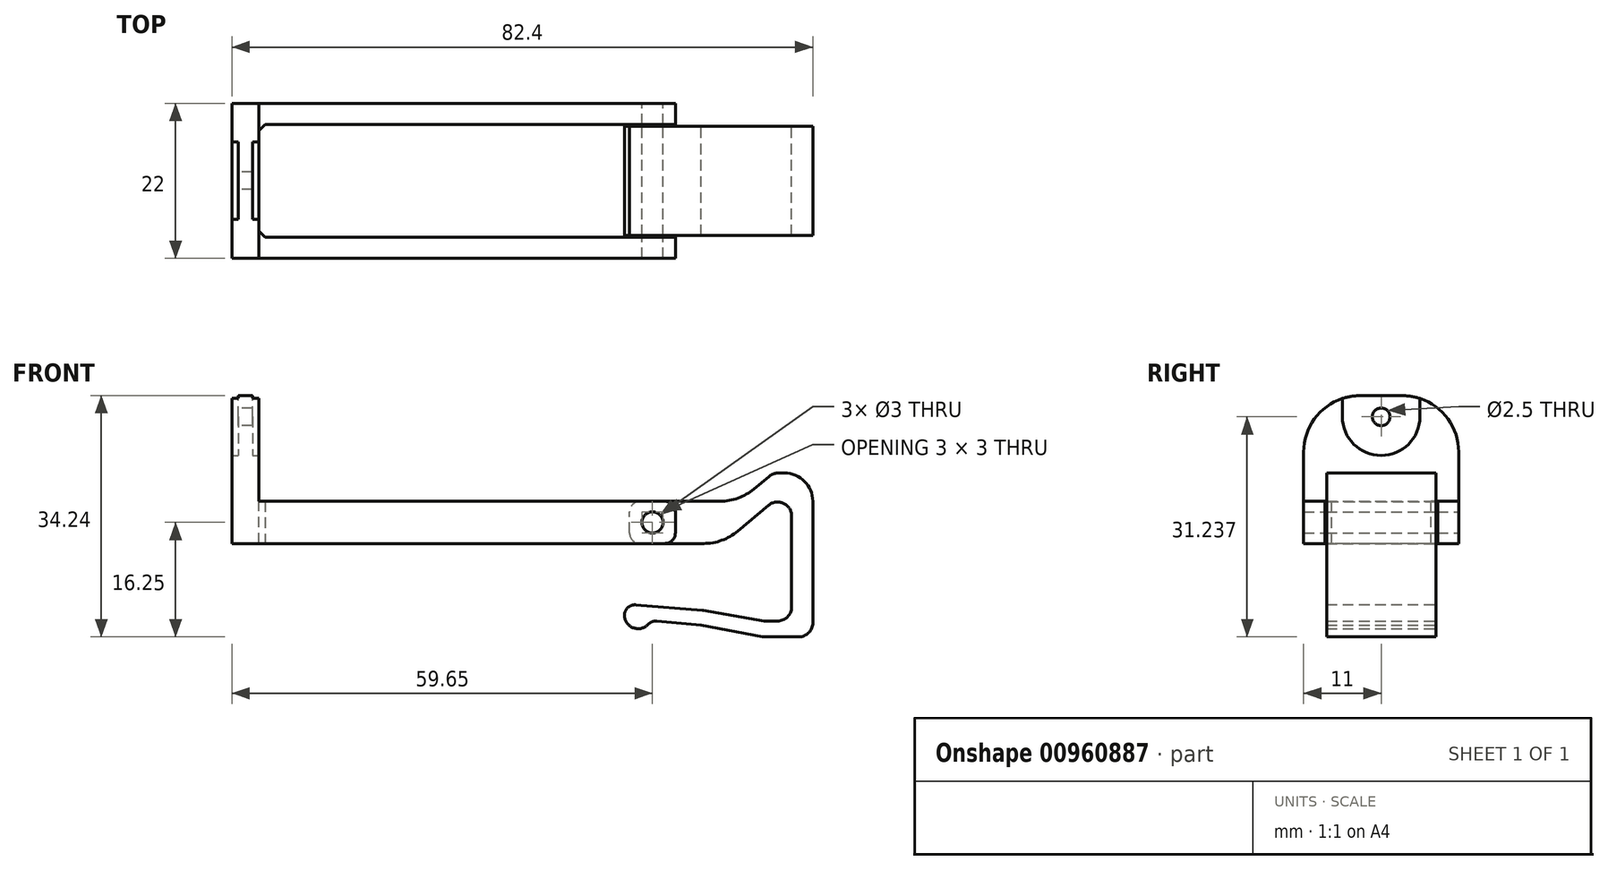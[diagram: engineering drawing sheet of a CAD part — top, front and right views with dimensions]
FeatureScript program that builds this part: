
annotation { "Feature Type Name" : "Feature", "Feature Type Description" : "" }
export const myFeature = defineFeature(function(context is Context, id is Id, definition is map)
    precondition{}
    {
        {
            var Q0;
            Q0=qCreatedBy(makeId("Right.planeOp"),FACE);
            var sketch = newSketch(context, id + "F0", { "sketchPlane" : qUnion([Q0])});
            skCircle(sketch, "E0", {"center": v(0, 17.99) * mm, "radius": 1.25 * mm});
            skLineSegment(sketch, "E1.bottom", {"start": v(-12.5, -0.01) * mm, "end": v(12.5, -0.01) * mm});
            skLineSegment(sketch, "E1.left", {"start": v(-11, -0.01) * mm, "end": v(-11, 12.99) * mm});
            skLineSegment(sketch, "E1.right", {"start": v(11, -0.01) * mm, "end": v(11, 12.99) * mm});
            skPoint(sketch, "E1.middle", {"position": v(0, 13) * mm});
            skLineSegment(sketch, "E2", {"start": v(12.5, 12.99) * mm, "end": v(-12.5, 12.99) * mm, "construction": true});
            skLineSegment(sketch, "E3", {"start": v(0, 4.99) * mm, "end": v(0, 20.99) * mm, "construction": true});
            skLineSegment(sketch, "E4.0", {"start": v(4.5, 4.99) * mm, "end": v(4.5, 20.99) * mm, "construction": true});
            skLineSegment(sketch, "E5.MirrorCS", {"start": v(-4.5, 4.99) * mm, "end": v(-4.5, 20.99) * mm, "construction": true});
            skLineSegment(sketch, "E6", {"start": v(5.5, 17.99) * mm, "end": v(-5.5, 17.99) * mm, "construction": true});
            skLineSegment(sketch, "E7", {"start": v(-5.5, 17.99) * mm, "end": v(-5.5, 20.92) * mm});
            skLineSegment(sketch, "E8.MirrorCS", {"start": v(5.5, 17.99) * mm, "end": v(5.5, 20.92) * mm});
            skArc(sketch, "E9", {"start": v(5.5, 17.99) * mm, "mid": v(0, 12.49) * mm, "end": v(-5.5, 17.99) * mm});
            skLineSegment(sketch, "E10", {"start": v(4.5, 20.99) * mm, "end": v(-4.5, 20.99) * mm});
            skPoint(sketch, "E11.middle", {"position": v(0, -0.01) * mm});
            skLineSegment(sketch, "E12.bottom", {"start": v(-20, 27.99) * mm, "end": v(20, 27.99) * mm});
            skLineSegment(sketch, "E12.top", {"start": v(-20, -7.01) * mm, "end": v(20, -7.01) * mm});
            skLineSegment(sketch, "E12.left", {"start": v(-20, 27.99) * mm, "end": v(-20, -7.01) * mm});
            skLineSegment(sketch, "E12.right", {"start": v(20, 27.99) * mm, "end": v(20, -7.01) * mm});
            skCircle(sketch, "E13", {"center": v(0, 0) * mm, "radius": 2.5 * mm, "construction": true});
            skArc(sketch, "E14", {"start": v(-11, 12.99) * mm, "mid": v(-9.17, 18.14) * mm, "end": v(-4.5, 20.99) * mm});
            skArc(sketch, "E15", {"start": v(11, 12.99) * mm, "mid": v(9.17, 18.14) * mm, "end": v(4.5, 20.99) * mm});
            skSolve(sketch);
        }
        {
            var Q0;
            Q0=qCreatedBy(makeId("Front.planeOp"),FACE);
            var sketch = newSketch(context, id + "F1", { "sketchPlane" : qUnion([Q0])});
            skPoint(sketch, "E16.middle", {"position": v(0, 8) * mm});
            skCircle(sketch, "E17", {"center": v(57.75, 3) * mm, "radius": 1.5 * mm});
            skArc(sketch, "E18", {"start": v(59.5, 0) * mm, "mid": v(60.56, 0.44) * mm, "end": v(61, 1.5) * mm});
            skArc(sketch, "E19.MirrorCS", {"start": v(59.5, 6) * mm, "mid": v(60.56, 5.56) * mm, "end": v(61, 4.5) * mm});
            skLineSegment(sketch, "E20", {"start": v(2, 6) * mm, "end": v(2, 21) * mm});
            skLineSegment(sketch, "E21", {"start": v(2, 21) * mm, "end": v(-2, 21) * mm});
            skLineSegment(sketch, "E22", {"start": v(-2, 21) * mm, "end": v(-2, 6) * mm});
            skLineSegment(sketch, "E23", {"start": v(-6.5, 0) * mm, "end": v(59.5, 0) * mm});
            skLineSegment(sketch, "E24", {"start": v(61, 4.5) * mm, "end": v(61, 1.5) * mm});
            skCircle(sketch, "E25", {"center": v(-4.75, 3) * mm, "radius": 1.5 * mm});
            skArc(sketch, "E26", {"start": v(-6.5, 6) * mm, "mid": v(-7.56, 5.56) * mm, "end": v(-8, 4.5) * mm});
            skArc(sketch, "E27.MirrorCS", {"start": v(-6.5, 0) * mm, "mid": v(-7.56, 0.44) * mm, "end": v(-8, 1.5) * mm});
            skLineSegment(sketch, "E28", {"start": v(-8, 1.5) * mm, "end": v(-8, 4.5) * mm});
            skLineSegment(sketch, "E29", {"start": v(59.5, 6) * mm, "end": v(2, 6) * mm});
            skLineSegment(sketch, "E30", {"start": v(-2, 6) * mm, "end": v(-6.5, 6) * mm});
            skSolve(sketch);
        }
        {
            var Q0;
            Q0=qCreatedBy(makeId("Top.planeOp"),FACE);
            var sketch = newSketch(context, id + "F2", { "sketchPlane" : qUnion([Q0])});
            skLineSegment(sketch, "E31.left", {"start": v(-2, 12.5) * mm, "end": v(-2, -12.5) * mm});
            skPoint(sketch, "E31.middle", {"position": v(56.25, 0) * mm});
            skLineSegment(sketch, "E32.0", {"start": v(2, 12.5) * mm, "end": v(2, -12.5) * mm});
            skLineSegment(sketch, "E33", {"start": v(-2, 0) * mm, "end": v(18.5, 0) * mm, "construction": true});
            skLineSegment(sketch, "E34.0", {"start": v(61, 11) * mm, "end": v(61, 8) * mm});
            skLineSegment(sketch, "E35.trimOffspring", {"start": v(61, -8) * mm, "end": v(61, -11) * mm});
            skLineSegment(sketch, "E36.bottom", {"start": v(69, 17.5) * mm, "end": v(-13, 17.5) * mm});
            skLineSegment(sketch, "E36.top", {"start": v(69, -17.5) * mm, "end": v(-13, -17.5) * mm});
            skLineSegment(sketch, "E36.left", {"start": v(69, 17.5) * mm, "end": v(69, -17.5) * mm});
            skLineSegment(sketch, "E36.right", {"start": v(-13, 17.5) * mm, "end": v(-13, -17.5) * mm});
            skPoint(sketch, "E36.middle", {"position": v(23, 0) * mm});
            skCircle(sketch, "E37", {"center": v(0, 0) * mm, "radius": 2.5 * mm, "construction": true});
            skLineSegment(sketch, "E38.0", {"start": v(61, -11) * mm, "end": v(-7.9, -11) * mm});
            skLineSegment(sketch, "E38.1", {"start": v(61, 11) * mm, "end": v(-7.9, 11) * mm});
            skLineSegment(sketch, "E38.2", {"start": v(-7.9, 8) * mm, "end": v(-2, 8) * mm});
            skLineSegment(sketch, "E38.3", {"start": v(-7.9, -8) * mm, "end": v(-2, -8) * mm});
            skCircle(sketch, "E38.4", {"center": v(23, 0) * mm, "radius": 2.5 * mm, "construction": true});
            skLineSegment(sketch, "E39", {"start": v(-7.9, 11) * mm, "end": v(-7.9, 8) * mm});
            skLineSegment(sketch, "E40", {"start": v(-7.9, -8) * mm, "end": v(-7.9, -11) * mm});
            skLineSegment(sketch, "E41", {"start": v(2, 8) * mm, "end": v(61, 8) * mm});
            skLineSegment(sketch, "E42", {"start": v(2, -8) * mm, "end": v(61, -8) * mm});
            skSolve(sketch);
        }
        {
            var Q0;
            Q0=qCreatedBy(makeId("Front.planeOp"),FACE);
            var sketch = newSketch(context, id + "F3", { "sketchPlane" : qUnion([Q0])});
            skCircle(sketch, "E43.0", {"center": v(57.75, 3) * mm, "radius": 1.5 * mm});
            skLineSegment(sketch, "E44.0", {"start": v(56, 0) * mm, "end": v(67.75, 0) * mm});
            skArc(sketch, "E44.1", {"start": v(56, 0) * mm, "mid": v(54.94, 0.44) * mm, "end": v(54.5, 1.5) * mm});
            skLineSegment(sketch, "E44.2", {"start": v(54.5, 1.5) * mm, "end": v(54.5, 4.5) * mm});
            skArc(sketch, "E44.3", {"start": v(56, 6) * mm, "mid": v(54.94, 5.56) * mm, "end": v(54.5, 4.5) * mm});
            skLineSegment(sketch, "E44.4", {"start": v(80.5, -13.25) * mm, "end": v(80.5, 10) * mm});
            skLineSegment(sketch, "E45", {"start": v(77.5, 8.18) * mm, "end": v(77.5, -11) * mm});
            skLineSegment(sketch, "E46", {"start": v(74.83, 10) * mm, "end": v(80.5, 10) * mm});
            skLineSegment(sketch, "E47", {"start": v(67.75, 0) * mm, "end": v(77.5, 8.18) * mm});
            skLineSegment(sketch, "E48", {"start": v(70.07, 6) * mm, "end": v(56, 6) * mm});
            skLineSegment(sketch, "E49", {"start": v(74.83, 10) * mm, "end": v(70.07, 6) * mm});
            skLineSegment(sketch, "E50", {"start": v(73.75, -11) * mm, "end": v(77.5, -11) * mm});
            skLineSegment(sketch, "E51", {"start": v(73.5, -13.25) * mm, "end": v(80.5, -13.25) * mm});
            skLineSegment(sketch, "E52", {"start": v(73.75, -11) * mm, "end": v(64.88, -9.48) * mm});
            skLineSegment(sketch, "E53", {"start": v(73.5, -13.25) * mm, "end": v(64.61, -11.61) * mm});
            skArc(sketch, "E54", {"start": v(54.5, -8.62) * mm, "mid": v(54.52, -11.68) * mm, "end": v(57.49, -10.93) * mm});
            skLineSegment(sketch, "E55", {"start": v(64.88, -9.48) * mm, "end": v(54.5, -8.62) * mm});
            skLineSegment(sketch, "E56", {"start": v(64.61, -11.61) * mm, "end": v(57.49, -10.93) * mm});
            skSolve(sketch);
        }
        {
            var Q0;
            Q0=makeQuery(id+"F1.imprint","IMPRINT",FACE,{"disambiguationData":[TD([[makeQuery(id+"F1.imprint","IMPRINT",EDGE,{"derivedFrom":sQuery(id+"F1.wireOp",EDGE,"E17")}),-1.0]])]});
            extrude(context, id + "F4", {"entities" : qUnion([Q0]), "endBound" : BoundingType.SYMMETRIC, "depth" : 25 * mm, "offsetDistance" : 25 * mm});
        }
        {
            var Q0;
            {var subQ16=sQuery(id+"F2.wireOp",EDGE,"E34.0");Q0=makeQuery(id+"F2.imprint","IMPRINT",FACE,{"disambiguationData":[TD([[makeQuery(id+"F2.imprint","IMPRINT",EDGE,{"derivedFrom":subQ16}),1.0]])]});}
            var Q1;
            {var subQ0=sQuery(id+"F2.wireOp",EDGE,"E38.2");Q1=makeQuery(id+"F2.imprint","IMPRINT",FACE,{"disambiguationData":[TD([[makeQuery(id+"F2.imprint","IMPRINT",EDGE,{"derivedFrom":subQ0}),1.0]])]});}
            var Q2;
            {var subQ3=sQuery(id+"F2.wireOp",EDGE,"E38.3");Q2=makeQuery(id+"F2.imprint","IMPRINT",FACE,{"disambiguationData":[TD([[makeQuery(id+"F2.imprint","IMPRINT",EDGE,{"derivedFrom":subQ3}),-1.0]])]});}
            extrude(context, id + "F5", {"entities" : qUnion([Q0, Q1, Q2]), "operationType" : NewBodyOperationType.REMOVE, "depth" : 25 * mm, "offsetDistance" : 25 * mm});
        }
        {
            var Q0;
            {var subQ11=sQuery(id+"F0.wireOp",EDGE,"E1.left");Q0=makeQuery(id+"F0.imprint","IMPRINT",FACE,{"disambiguationData":[TD([[makeQuery(id+"F0.imprint","IMPRINT",EDGE,{"derivedFrom":subQ11}),1.0]])]});}
            var Q1;
            {var subQ1=sQuery(id+"F0.wireOp",EDGE,"XXvW9FuW-Prl1-pEg8-0KIL-tEuXo7ml3rBn");var subQ3=sQuery(id+"F0.wireOp",EDGE,"E8.MirrorCS");var subQ4=makeQuery(id+"F0.imprint","INTERSECT",VERTEX,{"derivedFrom":[subQ1,subQ3]});Q1=makeQuery(id+"F0.imprint","IMPRINT",FACE,{"disambiguationData":[TD([[makeQuery(id+"F0.imprint","IMPRINT",EDGE,{"disambiguationData":[TD([[subQ4,1.0]])],"derivedFrom":subQ3}),1.0]])]});}
            var Q2;
            Q2=makeQuery(id+"F0.imprint","IMPRINT",FACE,{"disambiguationData":[TD([[makeQuery(id+"F0.imprint","IMPRINT",EDGE,{"derivedFrom":sQuery(id+"F0.wireOp",EDGE,"E0")}),-1.0]])]});
            var Q3;
            {var subQ1=sQuery(id+"F0.wireOp",EDGE,"gVsu0Bh6-VfbW-yezX-5lSl-KG5qwFbtLgBr");var subQ3=sQuery(id+"F0.wireOp",EDGE,"E7");var subQ4=makeQuery(id+"F0.imprint","INTERSECT",VERTEX,{"derivedFrom":[subQ1,subQ3]});Q3=makeQuery(id+"F0.imprint","IMPRINT",FACE,{"disambiguationData":[TD([[makeQuery(id+"F0.imprint","IMPRINT",EDGE,{"disambiguationData":[TD([[subQ4,1.0]])],"derivedFrom":subQ3}),-1.0]])]});}
            var Q4;
            Q4=makeQuery(id+"F0.imprint","IMPRINT",FACE,{"disambiguationData":[TD([[makeQuery(id+"F0.imprint","IMPRINT",EDGE,{"derivedFrom":sQuery(id+"F0.wireOp",EDGE,"E0")}),1.0]])]});
            extrude(context, id + "F6", {"entities" : qUnion([Q0, Q1, Q2, Q3, Q4]), "operationType" : NewBodyOperationType.REMOVE, "endBound" : BoundingType.SYMMETRIC, "oppositeDirection" : true, "depth" : 4 * mm, "offsetDistance" : 25 * mm});
        }
        {
            var Q0;
            Q0=makeQuery(id+"F0.imprint","IMPRINT",FACE,{"disambiguationData":[TD([[makeQuery(id+"F0.imprint","IMPRINT",EDGE,{"derivedFrom":sQuery(id+"F0.wireOp",EDGE,"E0")}),-1.0]])]});
            extrude(context, id + "F7", {"entities" : qUnion([Q0]), "operationType" : NewBodyOperationType.ADD, "endBound" : BoundingType.SYMMETRIC, "depth" : 2 * mm, "offsetDistance" : 25 * mm});
        }
        {
            var Q0;
            Q0=makeQuery(id+"F5.boolean.opBoolean","MERGE",FACE,{"derivedFrom":[makeQuery(id+"F4.opExtrude","SWEPT_FACE",FACE,{"disambiguationData":[OSD([sQuery(id+"F1.wireOp",EDGE,"E20")])]})],"fromTools":[makeQuery(id+"F5.opExtrude","SWEPT_FACE",FACE,{"disambiguationData":[OSD([sQuery(id+"F2.wireOp",EDGE,"E32.0")])]})]});
            extrude(context, id + "F8", {"entities" : qUnion([Q0]), "operationType" : NewBodyOperationType.REMOVE, "oppositeDirection" : true, "depth" : 0.1 * mm, "offsetDistance" : 25 * mm});
        }
        {
            var Q0;
            Q0=makeQuery(id+"F4.opExtrude","SWEPT_FACE",FACE,{"disambiguationData":[OSD([sQuery(id+"F1.wireOp",EDGE,"E22")])]});
            extrude(context, id + "F9", {"entities" : qUnion([Q0]), "operationType" : NewBodyOperationType.REMOVE, "oppositeDirection" : true, "depth" : 0.1 * mm, "offsetDistance" : 25 * mm});
        }
        {
            var Q0;
            Q0=makeQuery(id+"F8.boolean.opBoolean","COPY",EDGE,{"derivedFrom":makeQuery(id+"F8.opExtrude","CAP_EDGE",EDGE,{"disambiguationData":[OSD([sQuery(id+"F0.wireOp",EDGE,"E9")])],"isStart":false})});
            var Q1;
            Q1=makeQuery(id+"F9.boolean.opBoolean","COPY",EDGE,{"derivedFrom":makeQuery(id+"F9.opExtrude","CAP_EDGE",EDGE,{"disambiguationData":[OSD([sQuery(id+"F0.wireOp",EDGE,"E9")])],"isStart":false})});
            var Q2;
            Q2=makeQuery(id+"F9.boolean.opBoolean","COPY",EDGE,{"derivedFrom":makeQuery(id+"F9.opExtrude","CAP_EDGE",EDGE,{"disambiguationData":[OSD([sQuery(id+"F2.wireOp",EDGE,"E31.left"),sQuery(id+"F2.wireOp",EDGE,"E38.2")])],"isStart":false})});
            var Q3;
            Q3=makeQuery(id+"F9.boolean.opBoolean","COPY",EDGE,{"derivedFrom":makeQuery(id+"F9.opExtrude","CAP_EDGE",EDGE,{"disambiguationData":[OSD([sQuery(id+"F2.wireOp",EDGE,"E31.left"),sQuery(id+"F2.wireOp",EDGE,"E38.3")])],"isStart":false})});
            var Q4;
            Q4=makeQuery(id+"F8.boolean.opBoolean","COPY",EDGE,{"derivedFrom":makeQuery(id+"F8.opExtrude","CAP_EDGE",EDGE,{"disambiguationData":[OSD([sQuery(id+"F2.wireOp",EDGE,"E32.0"),sQuery(id+"F2.wireOp",EDGE,"E41")])],"isStart":false})});
            var Q5;
            Q5=makeQuery(id+"F8.boolean.opBoolean","COPY",EDGE,{"derivedFrom":makeQuery(id+"F8.opExtrude","CAP_EDGE",EDGE,{"disambiguationData":[OSD([sQuery(id+"F2.wireOp",EDGE,"E32.0"),sQuery(id+"F2.wireOp",EDGE,"E42")])],"isStart":false})});
            chamfer(context, id + "F10", {"entities" : qUnion([Q0, Q1, Q2, Q3, Q4, Q5]), "width" : 0.9 * mm, "tangentPropagation" : true});
        }
        {
            var Q0;
            Q0=makeQuery(id+"F3.imprint","IMPRINT",FACE,{"disambiguationData":[TD([[makeQuery(id+"F3.imprint","IMPRINT",EDGE,{"derivedFrom":sQuery(id+"F3.wireOp",EDGE,"E43.0")}),-1.0]])]});
            extrude(context, id + "F11", {"entities" : qUnion([Q0]), "endBound" : BoundingType.SYMMETRIC, "depth" : 15.5 * mm, "offsetDistance" : 25 * mm});
        }
        {
            var Q0;
            Q0=makeQuery(id+"F11.opExtrude","SWEPT_EDGE",EDGE,{"disambiguationData":[OSD([sQuery(id+"F3.wireOp",EDGE,"E46"),sQuery(id+"F3.wireOp",EDGE,"E49")])]});
            var Q1;
            Q1=makeQuery(id+"F11.opExtrude","SWEPT_EDGE",EDGE,{"disambiguationData":[OSD([sQuery(id+"F3.wireOp",EDGE,"E44.4"),sQuery(id+"F3.wireOp",EDGE,"E51")])]});
            var Q2;
            Q2=makeQuery(id+"F11.opExtrude","SWEPT_EDGE",EDGE,{"disambiguationData":[OSD([sQuery(id+"F3.wireOp",EDGE,"E45"),sQuery(id+"F3.wireOp",EDGE,"E50")])]});
            var Q3;
            Q3=makeQuery(id+"F11.opExtrude","SWEPT_EDGE",EDGE,{"disambiguationData":[OSD([sQuery(id+"F3.wireOp",EDGE,"E45"),sQuery(id+"F3.wireOp",EDGE,"E47")])]});
            var Q4;
            Q4=makeQuery(id+"F11.opExtrude","SWEPT_EDGE",EDGE,{"disambiguationData":[OSD([sQuery(id+"F3.wireOp",EDGE,"E44.4"),sQuery(id+"F3.wireOp",EDGE,"E51")])]});
            var Q5;
            Q5=makeQuery(id+"F11.opExtrude","SWEPT_EDGE",EDGE,{"disambiguationData":[OSD([sQuery(id+"F3.wireOp",EDGE,"E51"),sQuery(id+"F3.wireOp",EDGE,"f516b406-8fd0-4f9a-be36-c6f96f925c14")])]});
            var Q6;
            Q6=makeQuery(id+"F11.opExtrude","SWEPT_EDGE",EDGE,{"disambiguationData":[OSD([sQuery(id+"F3.wireOp",EDGE,"dadc7c79-95e2-4bde-80dc-f1ff961d30160.MirrorCS"),sQuery(id+"F3.wireOp",EDGE,"f516b406-8fd0-4f9a-be36-c6f96f925c14")])]});
            fillet(context, id + "F12", {"entities" : qUnion([Q0, Q1, Q2, Q3, Q4, Q5, Q6]), "tangentPropagation" : true, "radius" : 2 * mm, "defaultsChanged" : false, "vertexSettings" : [], "allowEdgeOverflow" : false});
        }
        {
            var Q0;
            Q0=makeQuery(id+"F11.opExtrude","SWEPT_EDGE",EDGE,{"disambiguationData":[OSD([sQuery(id+"F3.wireOp",EDGE,"E48"),sQuery(id+"F3.wireOp",EDGE,"E49")])]});
            var Q1;
            Q1=makeQuery(id+"F11.opExtrude","SWEPT_EDGE",EDGE,{"disambiguationData":[OSD([sQuery(id+"F3.wireOp",EDGE,"E44.0"),sQuery(id+"F3.wireOp",EDGE,"E47")])]});
            fillet(context, id + "F13", {"entities" : qUnion([Q0, Q1]), "tangentPropagation" : true, "radius" : 7.5 * mm, "defaultsChanged" : true, "vertexSettings" : [], "allowEdgeOverflow" : false});
        }
        {
            var Q0;
            Q0=makeQuery(id+"F11.opExtrude","SWEPT_EDGE",EDGE,{"disambiguationData":[OSD([sQuery(id+"F3.wireOp",EDGE,"E52"),sQuery(id+"F3.wireOp",EDGE,"E54")])]});
            fillet(context, id + "F14", {"entities" : qUnion([Q0]), "tangentPropagation" : true, "radius" : 1.5 * mm, "defaultsChanged" : true, "vertexSettings" : [], "allowEdgeOverflow" : false});
        }
        {
            var Q0;
            Q0=makeQuery(id+"F11.opExtrude","SWEPT_EDGE",EDGE,{"disambiguationData":[OSD([sQuery(id+"F3.wireOp",EDGE,"E44.4"),sQuery(id+"F3.wireOp",EDGE,"E46")])]});
            fillet(context, id + "F15", {"entities" : qUnion([Q0]), "tangentPropagation" : true, "radius" : 4 * mm, "defaultsChanged" : true, "vertexSettings" : [], "allowEdgeOverflow" : false});
        }
        {
            var Q0;
            Q0=makeQuery(id+"F7.opExtrude","SWEPT_EDGE",EDGE,{"disambiguationData":[OSD([sQuery(id+"F0.wireOp",EDGE,"XXvW9FuW-Prl1-pEg8-0KIL-tEuXo7ml3rBn"),sQuery(id+"F0.wireOp",EDGE,"E10"),sQuery(id+"F0.wireOp",EDGE,"E15")])]});
            var Q1;
            Q1=makeQuery(id+"F7.opExtrude","SWEPT_EDGE",EDGE,{"disambiguationData":[OSD([sQuery(id+"F0.wireOp",EDGE,"gVsu0Bh6-VfbW-yezX-5lSl-KG5qwFbtLgBr"),sQuery(id+"F0.wireOp",EDGE,"E10"),sQuery(id+"F0.wireOp",EDGE,"E14")])]});
            fillet(context, id + "F16", {"entities" : qUnion([Q0, Q1]), "tangentPropagation" : true, "radius" : 8 * mm, "defaultsChanged" : true, "vertexSettings" : [], "allowEdgeOverflow" : false});
        }
    });
